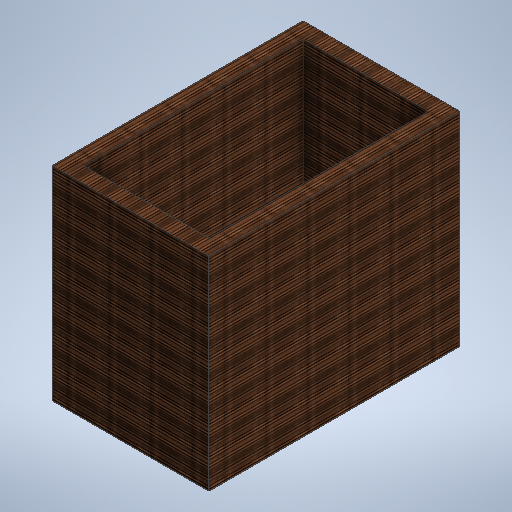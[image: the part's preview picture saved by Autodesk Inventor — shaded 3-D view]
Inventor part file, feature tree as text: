
AUTODESK INVENTOR PART (.ipt)
format: ipt  version: 2025.2 (Build 292293000, 293)  size: 457,728 bytes
history: native  units: mm
features: extrude x2, sketch x2, other x1
ambient origin geometry x8: Origin, YZ Plane, XZ Plane, XY Plane, X Axis, Y Axis, Z Axis, Center Point
bodies: Body1 (feature_tree)
feature tree (5):
  other  "Sólido1"
  extrude  "Extrusión1"  Depth=500.0mm
  extrude  "Extrusión2"  Depth=50.0mm
  sketch  "Boceto1"  dims[d0=800.0mm d1=500.0mm]
  sketch  "Boceto2"  dims[d2=50.0mm d3=50.0mm d6=600.0mm d7=0.0mm d8=50.0mm d9=0.0mm]
